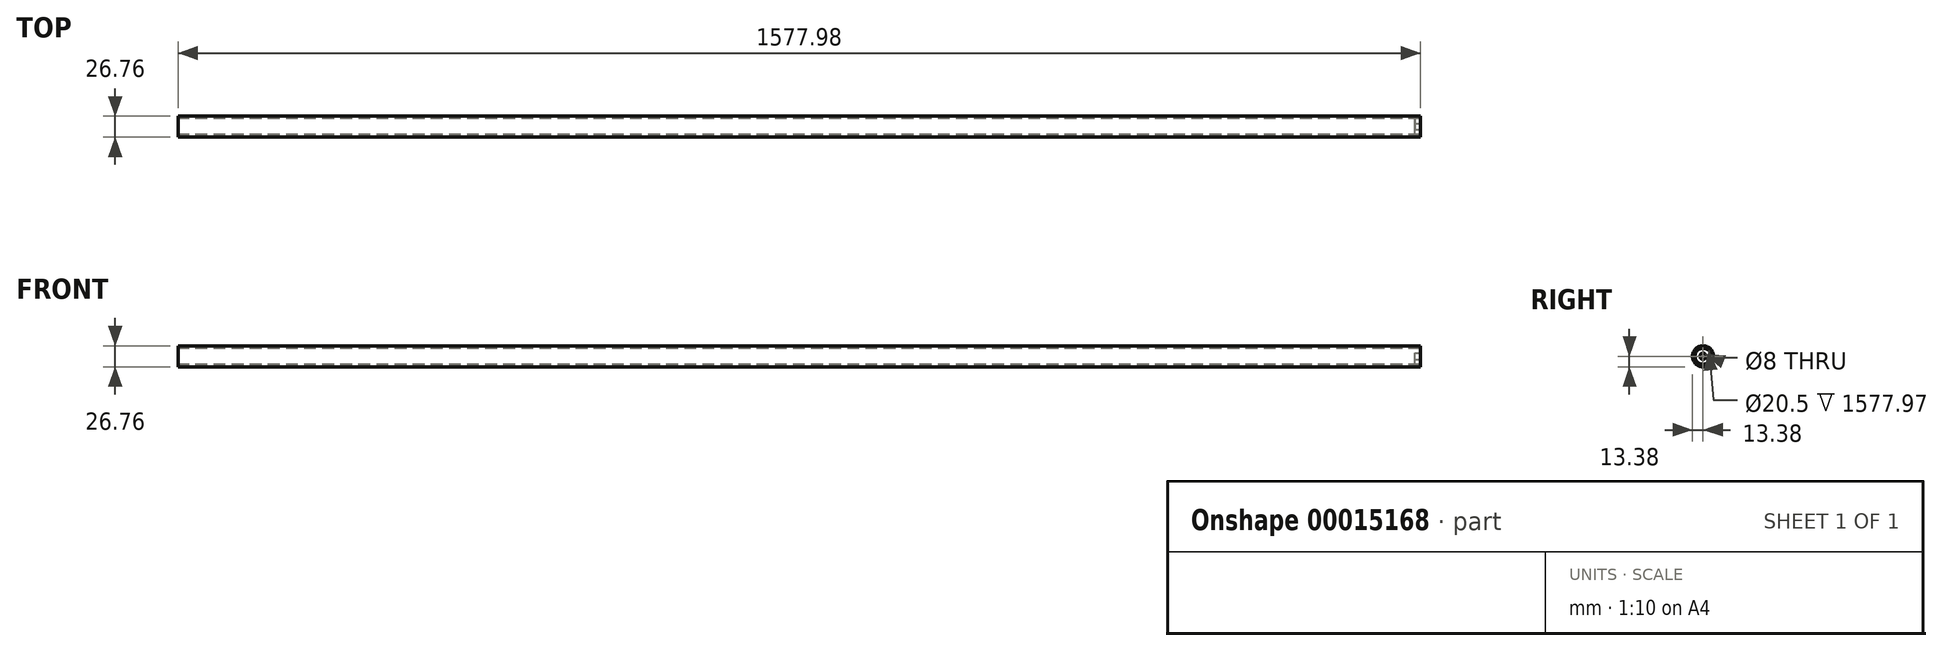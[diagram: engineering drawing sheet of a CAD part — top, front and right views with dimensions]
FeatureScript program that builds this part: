
annotation { "Feature Type Name" : "Feature", "Feature Type Description" : "" }
export const myFeature = defineFeature(function(context is Context, id is Id, definition is map)
    precondition{}
    {
        {
            var Q0;
            Q0=qCreatedBy(makeId("Right.planeOp"),FACE);
            var sketch = newSketch(context, id + "F0", { "sketchPlane" : qUnion([Q0])});
            skCircle(sketch, "E0", {"center": v(0, 0) * mm, "radius": 13.37 * mm});
            skCircle(sketch, "E1", {"center": v(0, 0) * mm, "radius": 10.25 * mm});
            skSolve(sketch);
        }
        {
            var Q0;
            Q0=makeQuery(id+"F0.imprint","IMPRINT",FACE,{"disambiguationData":[TD([[makeQuery(id+"F0.imprint","IMPRINT",EDGE,{"derivedFrom":sQuery(id+"F0.wireOp",EDGE,"E0")}),1.0]])]});
            extrude(context, id + "F1", {"entities" : qUnion([Q0]), "depth" : 1577.97 * mm});
        }
        {
            var Q0;
            Q0=makeQuery(id+"F1.opExtrude","CAP_FACE",FACE,{"disambiguationData":[OSD([sQuery(id+"F0.wireOp",EDGE,"E0"),sQuery(id+"F0.wireOp",EDGE,"E1")])],"isStart":false});
            var sketch = newSketch(context, id + "F2", { "sketchPlane" : qUnion([Q0])});
            skPoint(sketch, "E2.0", {"position": v(0, 0) * mm});
            skCircle(sketch, "E3.0", {"center": v(0, 0) * mm, "radius": 10.25 * mm});
            skCircle(sketch, "E4.0", {"center": v(0, 0) * mm, "radius": 13.37 * mm});
            skCircle(sketch, "E5", {"center": v(0, 0) * mm, "radius": 4 * mm});
            skCircle(sketch, "E6", {"center": v(0, 0) * mm, "radius": 11 * mm});
            skSolve(sketch);
        }
        {
            var Q0;
            Q0=makeQuery(id+"F2.imprint","IMPRINT",FACE,{"disambiguationData":[TD([[makeQuery(id+"F2.imprint","IMPRINT",EDGE,{"derivedFrom":sQuery(id+"F2.wireOp",EDGE,"E3.0")}),-1.0]])]});
            var Q1;
            Q1=makeQuery(id+"F2.imprint","IMPRINT",FACE,{"disambiguationData":[TD([[makeQuery(id+"F2.imprint","IMPRINT",EDGE,{"derivedFrom":sQuery(id+"F2.wireOp",EDGE,"E3.0")}),1.0]])]});
            extrude(context, id + "F3", {"entities" : qUnion([Q0, Q1]), "oppositeDirection" : true, "depth" : 7 * mm});
        }
    });
